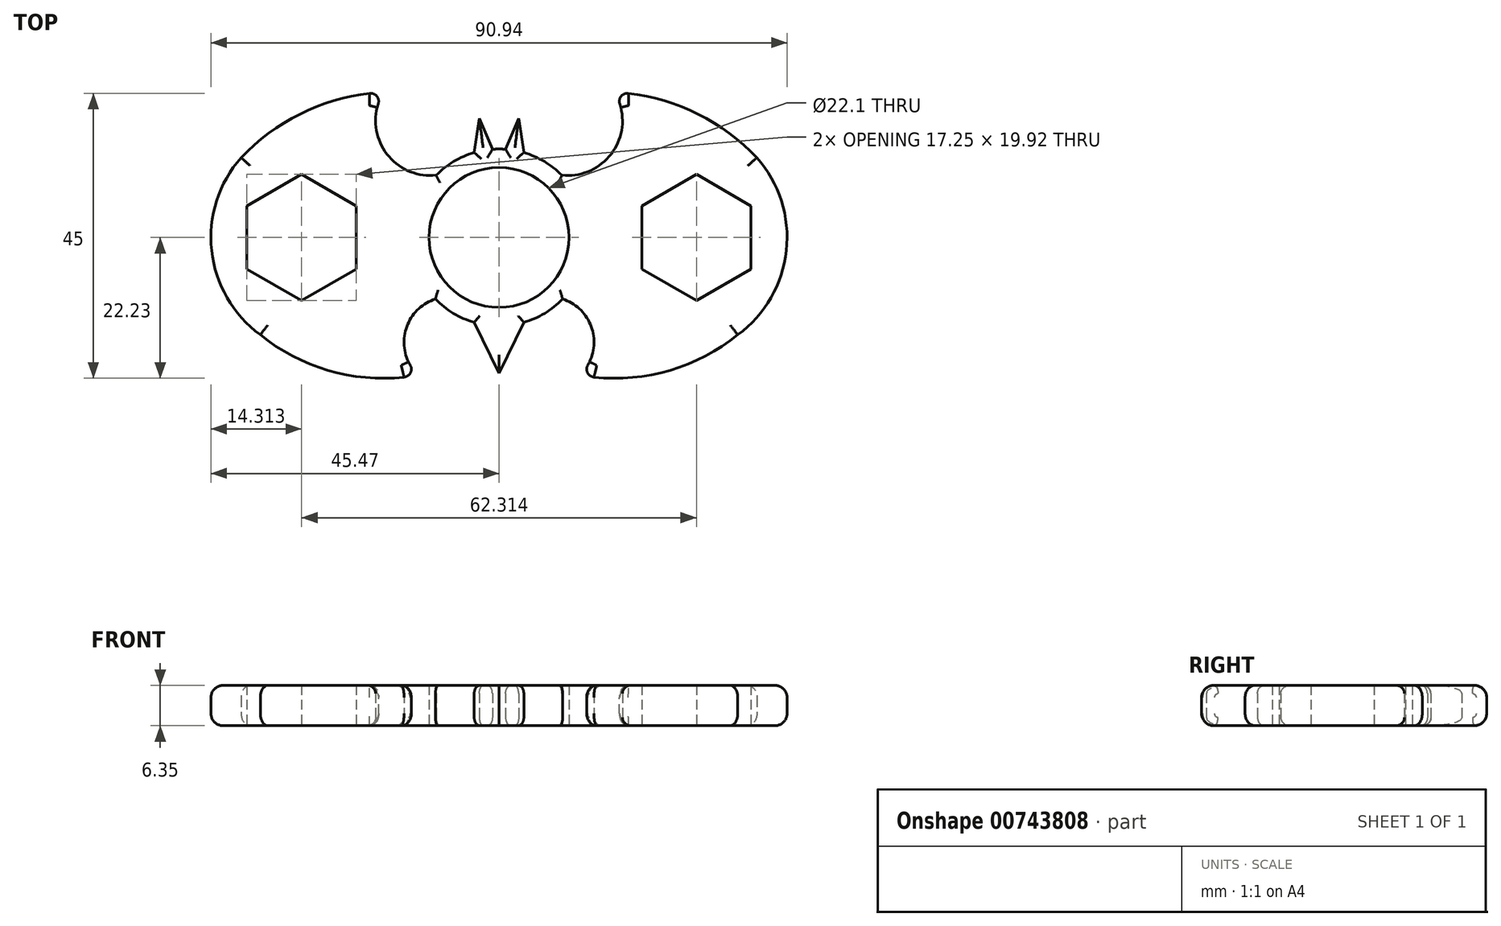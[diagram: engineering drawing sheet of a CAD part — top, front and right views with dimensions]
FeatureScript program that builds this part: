
annotation { "Feature Type Name" : "Feature", "Feature Type Description" : "" }
export const myFeature = defineFeature(function(context is Context, id is Id, definition is map)
    precondition{}
    {
        {
            var Q0;
            Q0=qCreatedBy(makeId("Top.planeOp"),FACE);
            var sketch = newSketch(context, id + "F0", { "sketchPlane" : qUnion([Q0])});
            skCircle(sketch, "E0", {"center": v(0, 0) * mm, "radius": 11.05 * mm});
            skCircle(sketch, "E1", {"center": v(0, 0) * mm, "radius": 13.97 * mm});
            skCircle(sketch, "E2", {"center": v(-31.16, 0) * mm, "radius": 9.53 * mm});
            skArc(sketch, "E3", {"start": v(37.68, -15.37) * mm, "mid": v(45.36, -2.05) * mm, "end": v(40.7, 12.6) * mm});
            skArc(sketch, "E4", {"start": v(-18.2, 22.95) * mm, "mid": v(-30.45, 19.93) * mm, "end": v(-40.7, 12.6) * mm});
            skArc(sketch, "E5", {"start": v(-18.2, 22.95) * mm, "mid": v(-18.15, 13.81) * mm, "end": v(-9.93, 9.83) * mm});
            skArc(sketch, "E6.trimOffspring", {"start": v(-40.7, 12.6) * mm, "mid": v(-45.36, -2.05) * mm, "end": v(-37.68, -15.37) * mm});
            skArc(sketch, "E7.MirrorCS", {"start": v(18.2, 22.95) * mm, "mid": v(18.15, 13.81) * mm, "end": v(9.93, 9.83) * mm});
            skArc(sketch, "E8.MirrorCS", {"start": v(18.2, 22.95) * mm, "mid": v(30.45, 19.93) * mm, "end": v(40.7, 12.6) * mm});
            skArc(sketch, "E9", {"start": v(-37.68, -15.37) * mm, "mid": v(-25.91, -21.27) * mm, "end": v(-12.76, -21.74) * mm});
            skArc(sketch, "E10", {"start": v(-10.03, -9.72) * mm, "mid": v(-14.81, -14.95) * mm, "end": v(-12.76, -21.74) * mm});
            skArc(sketch, "E11.MirrorCS", {"start": v(10.03, -9.72) * mm, "mid": v(14.81, -14.95) * mm, "end": v(12.76, -21.74) * mm});
            skArc(sketch, "E12.MirrorCS", {"start": v(37.68, -15.37) * mm, "mid": v(25.91, -21.27) * mm, "end": v(12.76, -21.74) * mm});
            skPoint(sketch, "E13.end.orphan", {"position": v(2.34, 18.82) * mm});
            skPoint(sketch, "E14.orphan", {"position": v(3.92, 13.4) * mm});
            skPoint(sketch, "E15.end.orphan", {"position": v(-1.04, 13.93) * mm});
            skPoint(sketch, "E16.end.orphan", {"position": v(-2.23, 18.82) * mm});
            skPoint(sketch, "E17.MirrorCS.end.orphan", {"position": v(1.04, 13.93) * mm});
            skPoint(sketch, "E17.MirrorCS.start.orphan", {"position": v(2.23, 18.82) * mm});
            skPoint(sketch, "E18.end.orphan", {"position": v(-4.8, 18.35) * mm});
            skPoint(sketch, "E19.MirrorCS.end.orphan", {"position": v(4.8, 18.35) * mm});
            skLineSegment(sketch, "E20", {"start": v(-1.04, 13.93) * mm, "end": v(-3.1, 18.83) * mm});
            skLineSegment(sketch, "E21", {"start": v(-3.1, 18.83) * mm, "end": v(-3.92, 13.4) * mm});
            skLineSegment(sketch, "E22.MirrorCS", {"start": v(1.04, 13.93) * mm, "end": v(3.1, 18.83) * mm});
            skLineSegment(sketch, "E23.MirrorCS", {"start": v(3.1, 18.83) * mm, "end": v(3.92, 13.4) * mm});
            skPoint(sketch, "E24.end.orphan", {"position": v(0, -21.45) * mm});
            skPoint(sketch, "E24.start.orphan", {"position": v(-4.01, -13.38) * mm});
            skPoint(sketch, "E25.MirrorCS.start.orphan", {"position": v(4.01, -13.38) * mm});
            skPoint(sketch, "E26.MirrorCS.end.orphan", {"position": v(-3.92, -13.4) * mm});
            skLineSegment(sketch, "E27", {"start": v(-3.92, -13.4) * mm, "end": v(0, -21.45) * mm});
            skLineSegment(sketch, "E28.MirrorCS", {"start": v(3.92, -13.4) * mm, "end": v(0, -21.45) * mm});
            skLineSegment(sketch, "E29", {"start": v(-26.42, 0) * mm, "end": v(-31.16, 0) * mm});
            skLineSegment(sketch, "E30", {"start": v(26.42, 0) * mm, "end": v(31.16, 0) * mm});
            skCircle(sketch, "E31.cCircle", {"center": v(-31.16, 0) * mm, "radius": 11.68 * mm, "construction": true});
            skLineSegment(sketch, "E31.0", {"start": v(-27.44, 12.97) * mm, "end": v(-18.07, 3.26) * mm});
            skLineSegment(sketch, "E31.1", {"start": v(-18.07, 3.26) * mm, "end": v(-21.79, -9.7) * mm});
            skLineSegment(sketch, "E31.2", {"start": v(-21.79, -9.7) * mm, "end": v(-34.87, -12.97) * mm});
            skLineSegment(sketch, "E31.3", {"start": v(-34.87, -12.97) * mm, "end": v(-44.24, -3.26) * mm});
            skLineSegment(sketch, "E31.4", {"start": v(-44.24, -3.26) * mm, "end": v(-40.53, 9.7) * mm});
            skLineSegment(sketch, "E31.5", {"start": v(-40.53, 9.7) * mm, "end": v(-27.44, 12.97) * mm});
            skPoint(sketch, "E31.0.midPoint", {"position": v(-22.75, 8.12) * mm});
            skCircle(sketch, "E32.cCircle", {"center": v(31.16, 0) * mm, "radius": 8.62 * mm, "construction": true});
            skLineSegment(sketch, "E32.0", {"start": v(31.16, 9.96) * mm, "end": v(39.78, 4.98) * mm});
            skLineSegment(sketch, "E32.1", {"start": v(39.78, 4.98) * mm, "end": v(39.78, -4.98) * mm});
            skLineSegment(sketch, "E32.2", {"start": v(39.78, -4.98) * mm, "end": v(31.16, -9.96) * mm});
            skLineSegment(sketch, "E32.3", {"start": v(31.16, -9.96) * mm, "end": v(22.53, -4.98) * mm});
            skLineSegment(sketch, "E32.4", {"start": v(22.53, -4.98) * mm, "end": v(22.53, 4.98) * mm});
            skLineSegment(sketch, "E32.5", {"start": v(22.53, 4.98) * mm, "end": v(31.16, 9.96) * mm});
            skPoint(sketch, "E32.0.midPoint", {"position": v(35.47, 7.47) * mm});
            skLineSegment(sketch, "E33", {"start": v(0, 24.66) * mm, "end": v(0, -28.67) * mm});
            skSolve(sketch);
        }
        {
            var Q0;
            {var subQ2=sQuery(id+"F0.wireOp",EDGE,"E33");var subQ7=sQuery(id+"F0.wireOp",EDGE,"E0");var subQ8=makeQuery(id+"F0.imprint","INTERSECT",VERTEX,{"disambiguationData":[OD(0.0)],"derivedFrom":[subQ7,subQ2]});Q0=makeQuery(id+"F0.imprint","IMPRINT",FACE,{"disambiguationData":[TD([[makeQuery(id+"F0.imprint","IMPRINT",EDGE,{"disambiguationData":[TD([[subQ8,1.0]])],"derivedFrom":subQ7}),-1.0]])]});}
            var Q1;
            {var subQ0=sQuery(id+"F0.wireOp",EDGE,"E22.MirrorCS");Q1=makeQuery(id+"F0.imprint","IMPRINT",FACE,{"disambiguationData":[TD([[makeQuery(id+"F0.imprint","IMPRINT",EDGE,{"derivedFrom":subQ0}),-1.0]])]});}
            var Q2;
            {var subQ0=sQuery(id+"F0.wireOp",EDGE,"E28.MirrorCS");Q2=makeQuery(id+"F0.imprint","IMPRINT",FACE,{"disambiguationData":[TD([[makeQuery(id+"F0.imprint","IMPRINT",EDGE,{"derivedFrom":subQ0}),-1.0]])]});}
            var Q3;
            Q3=makeQuery(id+"F0.imprint","IMPRINT",FACE,{"disambiguationData":[TD([[makeQuery(id+"F0.imprint","IMPRINT",EDGE,{"derivedFrom":sQuery(id+"F0.wireOp",EDGE,"E3")}),1.0]])]});
            extrude(context, id + "F1", {"entities" : qUnion([Q0, Q1, Q2, Q3]), "depth" : 6.35 * mm, "offsetDistance" : 25.4 * mm});
        }
        {
            var Q0;
            Q0=makeQuery(id+"F1.opExtrude","CAP_EDGE",EDGE,{"disambiguationData":[OSD([sQuery(id+"F0.wireOp",EDGE,"E6.trimOffspring")])],"isStart":false});
            var Q1;
            Q1=makeQuery(id+"F1.opExtrude","CAP_EDGE",EDGE,{"disambiguationData":[OSD([sQuery(id+"F0.wireOp",EDGE,"E3")])],"isStart":false});
            var Q2;
            Q2=makeQuery(id+"F1.opExtrude","CAP_EDGE",EDGE,{"disambiguationData":[OSD([sQuery(id+"F0.wireOp",EDGE,"E3")])],"isStart":true});
            var Q3;
            Q3=makeQuery(id+"F1.opExtrude","CAP_EDGE",EDGE,{"disambiguationData":[OSD([sQuery(id+"F0.wireOp",EDGE,"E6.trimOffspring")])],"isStart":true});
            fillet(context, id + "F2", {"entities" : qUnion([Q0, Q1, Q2, Q3]), "radius" : 1.9 * mm, "tangentPropagation" : true, "allowEdgeOverflow" : false});
        }
        {
            var Q0;
            Q0=makeQuery(id+"F2.opFillet","BLEND_EDGE",EDGE,{"blendedFrom":[makeQuery(id+"F1.opExtrude","CAP_EDGE",EDGE,{"disambiguationData":[OSD([sQuery(id+"F0.wireOp",EDGE,"E6.trimOffspring")])],"isStart":false}),makeQuery(id+"F1.opExtrude","SWEPT_FACE",FACE,{"disambiguationData":[OSD([sQuery(id+"F0.wireOp",EDGE,"E5")])]})],"blendedInto":[makeQuery(id+"F1.opExtrude","SWEPT_FACE",FACE,{"disambiguationData":[OSD([sQuery(id+"F0.wireOp",EDGE,"E5")])]})]});
            var Q1;
            Q1=makeQuery(id+"F2.opFillet","BLEND_EDGE",EDGE,{"blendedFrom":[makeQuery(id+"F1.opExtrude","CAP_EDGE",EDGE,{"disambiguationData":[OSD([sQuery(id+"F0.wireOp",EDGE,"E6.trimOffspring")])],"isStart":true}),makeQuery(id+"F1.opExtrude","SWEPT_FACE",FACE,{"disambiguationData":[OSD([sQuery(id+"F0.wireOp",EDGE,"E5")])]})],"blendedInto":[makeQuery(id+"F1.opExtrude","SWEPT_FACE",FACE,{"disambiguationData":[OSD([sQuery(id+"F0.wireOp",EDGE,"E5")])]})]});
            var Q2;
            Q2=makeQuery(id+"F1.opExtrude","CAP_EDGE",EDGE,{"disambiguationData":[OSD([sQuery(id+"F0.wireOp",EDGE,"E10")])],"isStart":false});
            var Q3;
            Q3=makeQuery(id+"F1.opExtrude","CAP_EDGE",EDGE,{"disambiguationData":[OSD([sQuery(id+"F0.wireOp",EDGE,"E11.MirrorCS")])],"isStart":false});
            var Q4;
            Q4=makeQuery(id+"F1.opExtrude","CAP_EDGE",EDGE,{"disambiguationData":[OSD([sQuery(id+"F0.wireOp",EDGE,"E7.MirrorCS")])],"isStart":false});
            var Q5;
            {var subQ0=sQuery(id+"F0.wireOp",EDGE,"E1");Q5=makeQuery(id+"F1.opExtrude","CAP_EDGE",EDGE,{"disambiguationData":[OSD([subQ0]),TDD([makeQuery(id+"F0.imprint","IMPRINT",EDGE,{"disambiguationData":[TD([[makeQuery(id+"F0.imprint","INTERSECT",VERTEX,{"derivedFrom":[subQ0,sQuery(id+"F0.wireOp",EDGE,"E5")]}),1.0]])],"derivedFrom":subQ0})])],"isStart":false});}
            var Q6;
            Q6=makeQuery(id+"F1.opExtrude","CAP_EDGE",EDGE,{"disambiguationData":[OSD([sQuery(id+"F0.wireOp",EDGE,"E21")])],"isStart":false});
            var Q7;
            {var subQ0=sQuery(id+"F0.wireOp",EDGE,"E1");Q7=makeQuery(id+"F1.opExtrude","CAP_EDGE",EDGE,{"disambiguationData":[OSD([subQ0]),TDD([makeQuery(id+"F0.imprint","IMPRINT",EDGE,{"disambiguationData":[TD([[makeQuery(id+"F0.imprint","INTERSECT",VERTEX,{"derivedFrom":[subQ0,sQuery(id+"F0.wireOp",EDGE,"E20")]}),1.0]])],"derivedFrom":subQ0})])],"isStart":false});}
            var Q8;
            Q8=makeQuery(id+"F1.opExtrude","CAP_EDGE",EDGE,{"disambiguationData":[OSD([sQuery(id+"F0.wireOp",EDGE,"E22.MirrorCS")])],"isStart":false});
            var Q9;
            {var subQ0=sQuery(id+"F0.wireOp",EDGE,"E1");Q9=makeQuery(id+"F1.opExtrude","CAP_EDGE",EDGE,{"disambiguationData":[OSD([subQ0]),TDD([makeQuery(id+"F0.imprint","IMPRINT",EDGE,{"disambiguationData":[TD([[makeQuery(id+"F0.imprint","INTERSECT",VERTEX,{"derivedFrom":[subQ0,sQuery(id+"F0.wireOp",EDGE,"E7.MirrorCS")]}),-1.0]])],"derivedFrom":subQ0})])],"isStart":false});}
            var Q10;
            {var subQ0=sQuery(id+"F0.wireOp",EDGE,"E1");Q10=makeQuery(id+"F1.opExtrude","CAP_EDGE",EDGE,{"disambiguationData":[OSD([subQ0]),TDD([makeQuery(id+"F0.imprint","IMPRINT",EDGE,{"disambiguationData":[TD([[makeQuery(id+"F0.imprint","INTERSECT",VERTEX,{"derivedFrom":[subQ0,sQuery(id+"F0.wireOp",EDGE,"E7.MirrorCS")]}),-1.0]])],"derivedFrom":subQ0})])],"isStart":true});}
            var Q11;
            Q11=makeQuery(id+"F1.opExtrude","CAP_EDGE",EDGE,{"disambiguationData":[OSD([sQuery(id+"F0.wireOp",EDGE,"E23.MirrorCS")])],"isStart":true});
            var Q12;
            {var subQ0=sQuery(id+"F0.wireOp",EDGE,"E1");Q12=makeQuery(id+"F1.opExtrude","CAP_EDGE",EDGE,{"disambiguationData":[OSD([subQ0]),TDD([makeQuery(id+"F0.imprint","IMPRINT",EDGE,{"disambiguationData":[TD([[makeQuery(id+"F0.imprint","INTERSECT",VERTEX,{"derivedFrom":[subQ0,sQuery(id+"F0.wireOp",EDGE,"E20")]}),1.0]])],"derivedFrom":subQ0})])],"isStart":true});}
            var Q13;
            Q13=makeQuery(id+"F1.opExtrude","CAP_EDGE",EDGE,{"disambiguationData":[OSD([sQuery(id+"F0.wireOp",EDGE,"E20")])],"isStart":true});
            var Q14;
            Q14=makeQuery(id+"F1.opExtrude","CAP_EDGE",EDGE,{"disambiguationData":[OSD([sQuery(id+"F0.wireOp",EDGE,"E21")])],"isStart":true});
            var Q15;
            {var subQ0=sQuery(id+"F0.wireOp",EDGE,"E1");Q15=makeQuery(id+"F1.opExtrude","CAP_EDGE",EDGE,{"disambiguationData":[OSD([subQ0]),TDD([makeQuery(id+"F0.imprint","IMPRINT",EDGE,{"disambiguationData":[TD([[makeQuery(id+"F0.imprint","INTERSECT",VERTEX,{"derivedFrom":[subQ0,sQuery(id+"F0.wireOp",EDGE,"E5")]}),1.0]])],"derivedFrom":subQ0})])],"isStart":true});}
            var Q16;
            {var subQ0=sQuery(id+"F0.wireOp",EDGE,"E1");Q16=makeQuery(id+"F1.opExtrude","CAP_EDGE",EDGE,{"disambiguationData":[OSD([subQ0]),TDD([makeQuery(id+"F0.imprint","IMPRINT",EDGE,{"disambiguationData":[TD([[makeQuery(id+"F0.imprint","INTERSECT",VERTEX,{"derivedFrom":[subQ0,sQuery(id+"F0.wireOp",EDGE,"E10")]}),-1.0]])],"derivedFrom":subQ0})])],"isStart":false});}
            var Q17;
            Q17=makeQuery(id+"F1.opExtrude","CAP_EDGE",EDGE,{"disambiguationData":[OSD([sQuery(id+"F0.wireOp",EDGE,"E27")])],"isStart":false});
            var Q18;
            Q18=makeQuery(id+"F1.opExtrude","CAP_EDGE",EDGE,{"disambiguationData":[OSD([sQuery(id+"F0.wireOp",EDGE,"E28.MirrorCS")])],"isStart":false});
            var Q19;
            {var subQ0=sQuery(id+"F0.wireOp",EDGE,"E1");Q19=makeQuery(id+"F1.opExtrude","CAP_EDGE",EDGE,{"disambiguationData":[OSD([subQ0]),TDD([makeQuery(id+"F0.imprint","IMPRINT",EDGE,{"disambiguationData":[TD([[makeQuery(id+"F0.imprint","INTERSECT",VERTEX,{"derivedFrom":[subQ0,sQuery(id+"F0.wireOp",EDGE,"E11.MirrorCS")]}),1.0]])],"derivedFrom":subQ0})])],"isStart":false});}
            var Q20;
            {var subQ0=sQuery(id+"F0.wireOp",EDGE,"E1");Q20=makeQuery(id+"F1.opExtrude","CAP_EDGE",EDGE,{"disambiguationData":[OSD([subQ0]),TDD([makeQuery(id+"F0.imprint","IMPRINT",EDGE,{"disambiguationData":[TD([[makeQuery(id+"F0.imprint","INTERSECT",VERTEX,{"derivedFrom":[subQ0,sQuery(id+"F0.wireOp",EDGE,"E11.MirrorCS")]}),1.0]])],"derivedFrom":subQ0})])],"isStart":true});}
            var Q21;
            Q21=makeQuery(id+"F1.opExtrude","CAP_EDGE",EDGE,{"disambiguationData":[OSD([sQuery(id+"F0.wireOp",EDGE,"E28.MirrorCS")])],"isStart":true});
            var Q22;
            Q22=makeQuery(id+"F1.opExtrude","CAP_EDGE",EDGE,{"disambiguationData":[OSD([sQuery(id+"F0.wireOp",EDGE,"E27")])],"isStart":true});
            var Q23;
            {var subQ0=sQuery(id+"F0.wireOp",EDGE,"E1");Q23=makeQuery(id+"F1.opExtrude","CAP_EDGE",EDGE,{"disambiguationData":[OSD([subQ0]),TDD([makeQuery(id+"F0.imprint","IMPRINT",EDGE,{"disambiguationData":[TD([[makeQuery(id+"F0.imprint","INTERSECT",VERTEX,{"derivedFrom":[subQ0,sQuery(id+"F0.wireOp",EDGE,"E10")]}),-1.0]])],"derivedFrom":subQ0})])],"isStart":true});}
            var Q24;
            Q24=makeQuery(id+"F1.opExtrude","CAP_EDGE",EDGE,{"disambiguationData":[OSD([sQuery(id+"F0.wireOp",EDGE,"E22.MirrorCS")])],"isStart":true});
            var Q25;
            Q25=makeQuery(id+"F1.opExtrude","CAP_EDGE",EDGE,{"disambiguationData":[OSD([sQuery(id+"F0.wireOp",EDGE,"E23.MirrorCS")])],"isStart":false});
            var Q26;
            Q26=makeQuery(id+"F1.opExtrude","CAP_EDGE",EDGE,{"disambiguationData":[OSD([sQuery(id+"F0.wireOp",EDGE,"E20")])],"isStart":false});
            var Q27;
            {var subQ0=sQuery(id+"F0.wireOp",EDGE,"E1");Q27=makeQuery(id+"F1.opExtrude","CAP_EDGE",EDGE,{"disambiguationData":[OSD([subQ0]),TDD([makeQuery(id+"F0.imprint","IMPRINT",EDGE,{"disambiguationData":[TD([[makeQuery(id+"F0.imprint","INTERSECT",VERTEX,{"derivedFrom":[subQ0,sQuery(id+"F0.wireOp",EDGE,"E22.MirrorCS")]}),-1.0]])],"derivedFrom":subQ0})])],"isStart":false});}
            var Q28;
            {var subQ0=sQuery(id+"F0.wireOp",EDGE,"E1");Q28=makeQuery(id+"F1.opExtrude","CAP_EDGE",EDGE,{"disambiguationData":[OSD([subQ0]),TDD([makeQuery(id+"F0.imprint","IMPRINT",EDGE,{"disambiguationData":[TD([[makeQuery(id+"F0.imprint","INTERSECT",VERTEX,{"derivedFrom":[subQ0,sQuery(id+"F0.wireOp",EDGE,"E22.MirrorCS")]}),-1.0]])],"derivedFrom":subQ0})])],"isStart":true});}
            fillet(context, id + "F3", {"entities" : qUnion([Q0, Q1, Q2, Q3, Q4, Q5, Q6, Q7, Q8, Q9, Q10, Q11, Q12, Q13, Q14, Q15, Q16, Q17, Q18, Q19, Q20, Q21, Q22, Q23, Q24, Q25, Q26, Q27, Q28]), "radius" : 1.27 * mm, "tangentPropagation" : true, "allowEdgeOverflow" : false});
        }
        {
            var Q0;
            Q0=makeQuery(id+"F1.opExtrude","SWEPT_BODY",BODY,{"disambiguationData":[OSD([sQuery(id+"F0.wireOp",EDGE,"E0"),sQuery(id+"F0.wireOp",EDGE,"E1"),sQuery(id+"F0.wireOp",EDGE,"E3"),sQuery(id+"F0.wireOp",EDGE,"E7.MirrorCS"),sQuery(id+"F0.wireOp",EDGE,"E8.MirrorCS"),sQuery(id+"F0.wireOp",EDGE,"E11.MirrorCS"),sQuery(id+"F0.wireOp",EDGE,"E12.MirrorCS"),sQuery(id+"F0.wireOp",EDGE,"E22.MirrorCS"),sQuery(id+"F0.wireOp",EDGE,"E23.MirrorCS"),sQuery(id+"F0.wireOp",EDGE,"E28.MirrorCS"),sQuery(id+"F0.wireOp",EDGE,"E32.0"),sQuery(id+"F0.wireOp",EDGE,"E32.1"),sQuery(id+"F0.wireOp",EDGE,"E32.2"),sQuery(id+"F0.wireOp",EDGE,"E32.3"),sQuery(id+"F0.wireOp",EDGE,"E32.4"),sQuery(id+"F0.wireOp",EDGE,"E32.5"),sQuery(id+"F0.wireOp",EDGE,"E33")])]});
            var Q1;
            {var subQ0=sQuery(id+"F0.wireOp",EDGE,"E33");var subQ1=makeQuery(id+"F0.imprint","INTERSECT",VERTEX,{"disambiguationData":[OD(1.0)],"derivedFrom":[sQuery(id+"F0.wireOp",EDGE,"E1"),subQ0]});Q1=makeQuery(id+"F1.opExtrude","SWEPT_FACE",FACE,{"disambiguationData":[OSD([subQ0]),TDD([makeQuery(id+"F0.imprint","IMPRINT",EDGE,{"disambiguationData":[TD([[makeQuery(id+"F0.imprint","INTERSECT",VERTEX,{"disambiguationData":[OD(1.0)],"derivedFrom":[sQuery(id+"F0.wireOp",EDGE,"E0"),subQ0]}),-1.0]])],"derivedFrom":subQ0}),makeQuery(id+"F0.imprint","IMPRINT",EDGE,{"disambiguationData":[TD([[subQ1,-1.0]])],"derivedFrom":subQ0})])]});}
            mirror(context, id + "F4", {"operationType" : NewBodyOperationType.ADD, "entities" : qUnion([Q0]), "mirrorPlane" : qUnion([Q1])});
        }
    });
